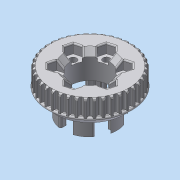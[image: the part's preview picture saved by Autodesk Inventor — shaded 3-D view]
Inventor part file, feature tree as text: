
AUTODESK INVENTOR PART (.ipt)
format: ipt  version: 2014 SP1 (Build 180222100, 222)  size: 2,058,240 bytes
history: native  units: in
note: dims shown in document units (in); Inventor stores cm internally (conversion verified against a paired STEP export)
features: sketch x6, other x4
ambient origin geometry x8: Origin, YZ Plane, XZ Plane, XY Plane, X Axis, Y Axis, Z Axis, Center Point
bodies: Solid1 (feature_tree), Solid2 (feature_tree)
feature tree (10):
  other  "wheelinsertinner40t.ipt"
  other  "Solid1::wheelinsertinner40t.ipt"
  other  "Solid3::wheelinsertinner40t.ipt"
  other  "TaggingFeature1"
  sketch  "Sketch1"  dims[d0=0.3937in]
  sketch  "Sketch14"
  sketch  "Sketch13"
  sketch  "Sketch6"  dims[d1=0.5in d2=0.0in d3=2.4803in d4=0.3in d5=0.0in d6=0.25in d34=0.3937in d35=90.0deg d36=0.0in d37=-2.0in d38=0.0in d39=1.1in d41=0.0in d42=5.0in d43=0.0in d44=0.05in d45=0.02in d46=0.125in d61=0.1625in d80=0.38in d81=2.3622in d86=0.0in d87=0.2756in d88=0.0in d90=0.4724in d91=0.0in d92=0.0591in d96=0.0394in d102=0.205in d103=0.0787in d83=360.0deg]
  sketch  "Sketch7"
  sketch  "Sketch12"
